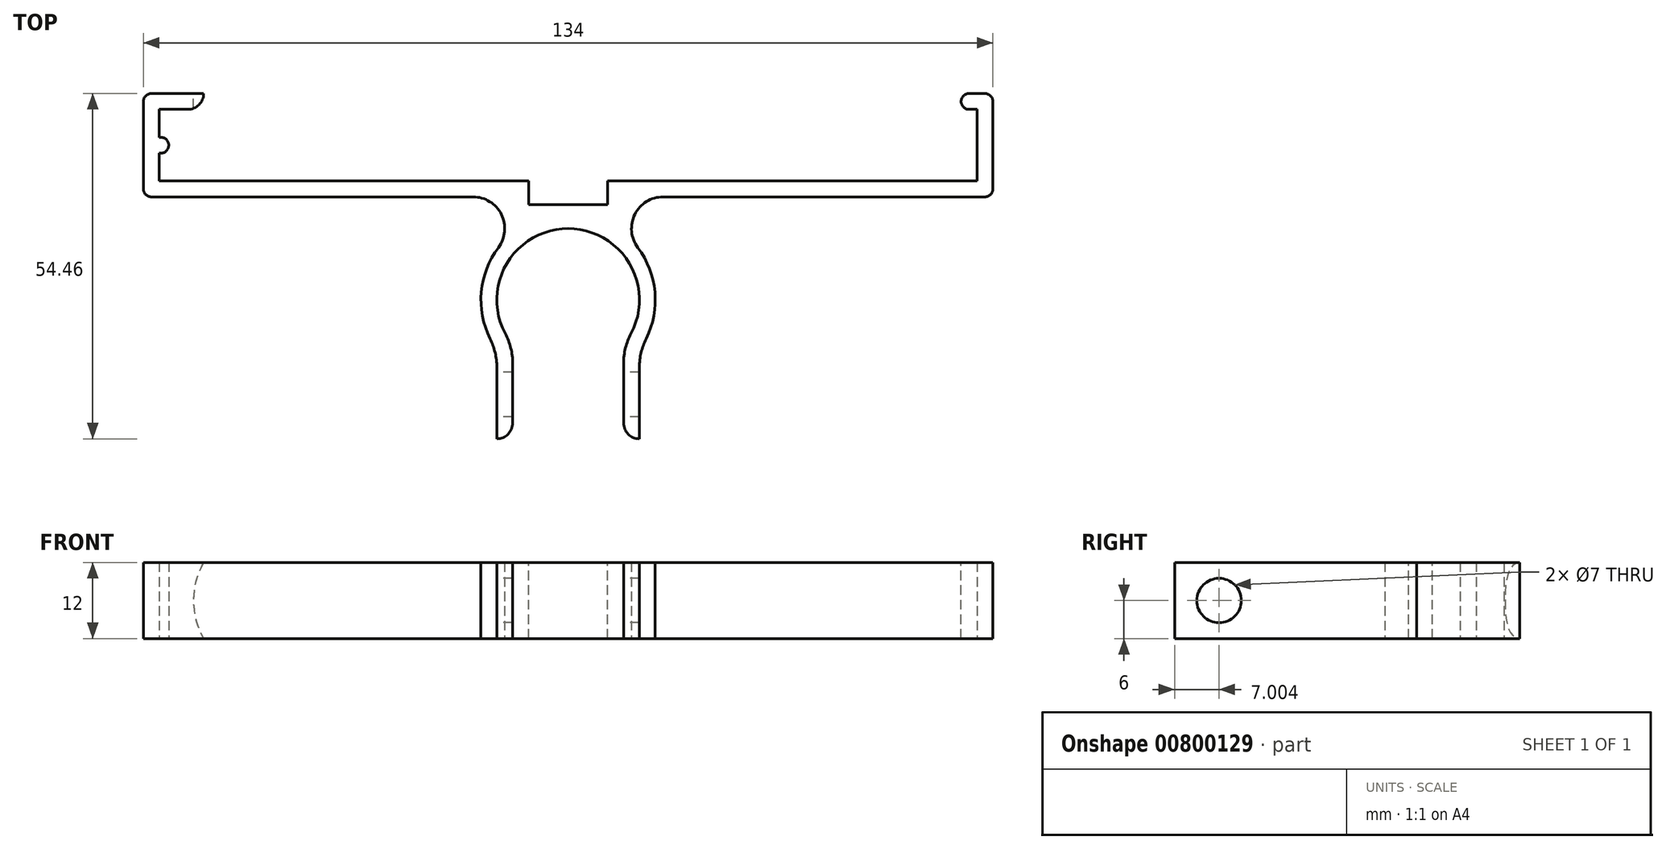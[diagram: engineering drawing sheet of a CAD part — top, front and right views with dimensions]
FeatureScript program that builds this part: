
annotation { "Feature Type Name" : "Feature", "Feature Type Description" : "" }
export const myFeature = defineFeature(function(context is Context, id is Id, definition is map)
    precondition{}
    {
        {
            var Q0;
            Q0=qCreatedBy(makeId("Top.planeOp"),FACE);
            var sketch = newSketch(context, id + "F0", { "sketchPlane" : qUnion([Q0])});
            skArc(sketch, "E0", {"start": v(8.75, -7.07) * mm, "mid": v(0, 11.25) * mm, "end": v(-8.75, -7.07) * mm});
            skArc(sketch, "E1.0", {"start": v(8.75, -10.6) * mm, "mid": v(0, 13.75) * mm, "end": v(-8.75, -10.6) * mm});
            skLineSegment(sketch, "E2", {"start": v(-11.25, 0) * mm, "end": v(-11.25, -21.9) * mm});
            skLineSegment(sketch, "E3", {"start": v(-11.25, -21.9) * mm, "end": v(-8.75, -21.9) * mm});
            skLineSegment(sketch, "E4", {"start": v(-8.75, -21.9) * mm, "end": v(-8.75, -7.07) * mm});
            skPoint(sketch, "E5", {"position": v(-11.25, -7.9) * mm});
            skLineSegment(sketch, "E6.bottom", {"start": v(64.5, 16.25) * mm, "end": v(-64.5, 16.25) * mm});
            skLineSegment(sketch, "E6.top", {"start": v(64.5, 18.75) * mm, "end": v(-64.5, 18.75) * mm});
            skLineSegment(sketch, "E6.left", {"start": v(64.5, 16.25) * mm, "end": v(64.5, 18.75) * mm});
            skPoint(sketch, "E6.middle", {"position": v(0, 17.5) * mm});
            skArc(sketch, "E7", {"start": v(-11, 8.25) * mm, "mid": v(-10.53, 13.49) * mm, "end": v(-15, 16.25) * mm});
            skLineSegment(sketch, "E8.bottom", {"start": v(-64.5, 16.25) * mm, "end": v(-67, 16.25) * mm});
            skLineSegment(sketch, "E8.top", {"start": v(-64.5, 30.05) * mm, "end": v(-67, 30.05) * mm});
            skLineSegment(sketch, "E8.left", {"start": v(-64.5, 18.75) * mm, "end": v(-64.5, 30.05) * mm});
            skLineSegment(sketch, "E8.right", {"start": v(-67, 16.25) * mm, "end": v(-67, 30.05) * mm});
            skLineSegment(sketch, "E9.MirrorCS", {"start": v(8.75, -21.9) * mm, "end": v(8.75, -7.07) * mm});
            skLineSegment(sketch, "E10.MirrorCS", {"start": v(11.25, 0) * mm, "end": v(11.25, -21.9) * mm});
            skLineSegment(sketch, "E11.MirrorCS", {"start": v(11.25, -21.9) * mm, "end": v(8.75, -21.9) * mm});
            skLineSegment(sketch, "E12.MirrorCS", {"start": v(67, 16.25) * mm, "end": v(67, 30.05) * mm});
            skLineSegment(sketch, "E13.MirrorCS", {"start": v(64.5, 16.25) * mm, "end": v(64.5, 30.05) * mm});
            skLineSegment(sketch, "E14.MirrorCS", {"start": v(64.5, 30.05) * mm, "end": v(67, 30.05) * mm});
            skLineSegment(sketch, "E15.MirrorCS", {"start": v(64.5, 16.25) * mm, "end": v(67, 16.25) * mm});
            skLineSegment(sketch, "E16.bottom", {"start": v(-67, 30.05) * mm, "end": v(-57.5, 30.05) * mm});
            skLineSegment(sketch, "E16.top", {"start": v(-67, 32.55) * mm, "end": v(-57.5, 32.55) * mm});
            skLineSegment(sketch, "E16.left", {"start": v(-67, 30.05) * mm, "end": v(-67, 32.55) * mm});
            skLineSegment(sketch, "E16.right", {"start": v(-57.5, 30.05) * mm, "end": v(-57.5, 32.55) * mm});
            skLineSegment(sketch, "E17.trimOffspring", {"start": v(0, 18.75) * mm, "end": v(-64.5, 18.75) * mm});
            skLineSegment(sketch, "E18.bottom", {"start": v(-64.5, 23.15) * mm, "end": v(-63, 23.15) * mm});
            skLineSegment(sketch, "E18.top", {"start": v(-64.5, 25.65) * mm, "end": v(-63, 25.65) * mm});
            skLineSegment(sketch, "E18.left", {"start": v(-64.5, 23.15) * mm, "end": v(-64.5, 25.65) * mm});
            skLineSegment(sketch, "E18.right", {"start": v(-63, 23.15) * mm, "end": v(-63, 25.65) * mm});
            skPoint(sketch, "E19", {"position": v(-64.5, 24.4) * mm});
            skLineSegment(sketch, "E20.bottom", {"start": v(67, 30.05) * mm, "end": v(62, 30.05) * mm});
            skLineSegment(sketch, "E20.top", {"start": v(67, 32.55) * mm, "end": v(62, 32.55) * mm});
            skLineSegment(sketch, "E20.left", {"start": v(67, 30.05) * mm, "end": v(67, 32.55) * mm});
            skLineSegment(sketch, "E20.right", {"start": v(62, 30.05) * mm, "end": v(62, 32.55) * mm});
            skArc(sketch, "E21.MirrorCS", {"start": v(11, 8.25) * mm, "mid": v(10.53, 13.49) * mm, "end": v(15, 16.25) * mm});
            skSolve(sketch);
        }
        {
            var Q0;
            Q0 = qSketchRegion(id + "F0", true);
            extrude(context, id + "F1", {"entities" : qUnion([Q0]), "depth" : 12 * mm, "offsetDistance" : 25 * mm});
        }
        {
            var Q0;
            Q0=makeQuery(id+"F1.opExtrude","SWEPT_FACE",FACE,{"disambiguationData":[OSD([sQuery(id+"F0.wireOp",EDGE,"E2")])]});
            var sketch = newSketch(context, id + "F2", { "sketchPlane" : qUnion([Q0])});
            skCircle(sketch, "E22", {"center": v(14.9, 6) * mm, "radius": 3.5 * mm});
            skSolve(sketch);
        }
        {
            var Q0;
            Q0=makeQuery(id+"F2.imprint","IMPRINT",FACE,{"disambiguationData":[TD([[makeQuery(id+"F2.imprint","IMPRINT",EDGE,{"derivedFrom":sQuery(id+"F2.wireOp",EDGE,"E22")}),1.0]])]});
            var Q1;
            Q1=sQuery(id+"F2.wireOp",EDGE,"E22");
            var Q2;
            Q2=makeQuery(id+"F1.opExtrude","SWEPT_FACE",FACE,{"disambiguationData":[OSD([sQuery(id+"F0.wireOp",EDGE,"E10.MirrorCS")])]});
            extrude(context, id + "F3", {"entities" : qUnion([Q0]), "operationType" : NewBodyOperationType.REMOVE, "surfaceEntities" : qUnion([Q1]), "endBound" : BoundingType.UP_TO_SURFACE, "oppositeDirection" : true, "depth" : 25 * mm, "endBoundEntityFace" : qUnion([Q2]), "offsetDistance" : 25 * mm});
        }
        {
            var Q0;
            Q0=makeQuery(id+"F1.opExtrude","SWEPT_EDGE",EDGE,{"disambiguationData":[OSD([sQuery(id+"F0.wireOp",EDGE,"E0"),sQuery(id+"F0.wireOp",EDGE,"E4")])]});
            var Q1;
            Q1=makeQuery(id+"F1.opExtrude","SWEPT_EDGE",EDGE,{"disambiguationData":[OSD([sQuery(id+"F0.wireOp",EDGE,"E0"),sQuery(id+"F0.wireOp",EDGE,"E9.MirrorCS")])]});
            var Q2;
            Q2=makeQuery(id+"F1.opExtrude","SWEPT_EDGE",EDGE,{"disambiguationData":[OSD([sQuery(id+"F0.wireOp",EDGE,"E1.0"),sQuery(id+"F0.wireOp",EDGE,"E2")])]});
            var Q3;
            Q3=makeQuery(id+"F1.opExtrude","SWEPT_EDGE",EDGE,{"disambiguationData":[OSD([sQuery(id+"F0.wireOp",EDGE,"E1.0"),sQuery(id+"F0.wireOp",EDGE,"E10.MirrorCS")])]});
            fillet(context, id + "F4", {"entities" : qUnion([Q0, Q1, Q2, Q3]), "radius" : 10 * mm, "tangentPropagation" : true, "allowEdgeOverflow" : false});
        }
        {
            var Q0;
            Q0=makeQuery(id+"F1.opExtrude","SWEPT_EDGE",EDGE,{"disambiguationData":[OSD([sQuery(id+"F0.wireOp",EDGE,"E16.bottom"),sQuery(id+"F0.wireOp",EDGE,"E16.right")])]});
            var Q1;
            Q1=makeQuery(id+"F1.opExtrude","SWEPT_EDGE",EDGE,{"disambiguationData":[OSD([sQuery(id+"F0.wireOp",EDGE,"E3"),sQuery(id+"F0.wireOp",EDGE,"E4")])]});
            var Q2;
            Q2=makeQuery(id+"F1.opExtrude","SWEPT_EDGE",EDGE,{"disambiguationData":[OSD([sQuery(id+"F0.wireOp",EDGE,"E9.MirrorCS"),sQuery(id+"F0.wireOp",EDGE,"E11.MirrorCS")])]});
            fillet(context, id + "F5", {"entities" : qUnion([Q0, Q1, Q2]), "radius" : 2.5 * mm, "tangentPropagation" : true, "allowEdgeOverflow" : false});
        }
        {
            var Q0;
            Q0=makeQuery(id+"F1.opExtrude","SWEPT_EDGE",EDGE,{"disambiguationData":[OSD([sQuery(id+"F0.wireOp",EDGE,"E16.top"),sQuery(id+"F0.wireOp",EDGE,"E16.left")])]});
            var Q1;
            Q1=makeQuery(id+"F1.opExtrude","SWEPT_EDGE",EDGE,{"disambiguationData":[OSD([sQuery(id+"F0.wireOp",EDGE,"E8.bottom"),sQuery(id+"F0.wireOp",EDGE,"E8.right")])]});
            var Q2;
            Q2=makeQuery(id+"F1.opExtrude","SWEPT_EDGE",EDGE,{"disambiguationData":[OSD([sQuery(id+"F0.wireOp",EDGE,"E12.MirrorCS"),sQuery(id+"F0.wireOp",EDGE,"E15.MirrorCS")])]});
            var Q3;
            Q3=makeQuery(id+"F1.opExtrude","SWEPT_EDGE",EDGE,{"disambiguationData":[OSD([sQuery(id+"F0.wireOp",EDGE,"E18.bottom"),sQuery(id+"F0.wireOp",EDGE,"E18.right")])]});
            var Q4;
            Q4=makeQuery(id+"F1.opExtrude","SWEPT_EDGE",EDGE,{"disambiguationData":[OSD([sQuery(id+"F0.wireOp",EDGE,"E18.top"),sQuery(id+"F0.wireOp",EDGE,"E18.right")])]});
            var Q5;
            Q5=makeQuery(id+"F1.opExtrude","SWEPT_EDGE",EDGE,{"disambiguationData":[OSD([sQuery(id+"F0.wireOp",EDGE,"E20.top"),sQuery(id+"F0.wireOp",EDGE,"E20.right")])]});
            var Q6;
            Q6=makeQuery(id+"F1.opExtrude","SWEPT_EDGE",EDGE,{"disambiguationData":[OSD([sQuery(id+"F0.wireOp",EDGE,"E20.bottom"),sQuery(id+"F0.wireOp",EDGE,"E20.right")])]});
            var Q7;
            Q7=makeQuery(id+"F1.opExtrude","SWEPT_EDGE",EDGE,{"disambiguationData":[OSD([sQuery(id+"F0.wireOp",EDGE,"E20.top"),sQuery(id+"F0.wireOp",EDGE,"E20.left")])]});
            fillet(context, id + "F6", {"entities" : qUnion([Q0, Q1, Q2, Q3, Q4, Q5, Q6, Q7]), "radius" : 1.25 * mm, "tangentPropagation" : true, "allowEdgeOverflow" : false});
        }
        {
            var Q0;
            Q0=makeQuery(id+"F1.opExtrude","CAP_FACE",FACE,{"disambiguationData":[OSD([sQuery(id+"F0.wireOp",EDGE,"E0"),sQuery(id+"F0.wireOp",EDGE,"E1.0"),sQuery(id+"F0.wireOp",EDGE,"E2"),sQuery(id+"F0.wireOp",EDGE,"E3"),sQuery(id+"F0.wireOp",EDGE,"E4"),sQuery(id+"F0.wireOp",EDGE,"E6.bottom"),sQuery(id+"F0.wireOp",EDGE,"E6.top"),sQuery(id+"F0.wireOp",EDGE,"E7"),sQuery(id+"F0.wireOp",EDGE,"E8.bottom"),sQuery(id+"F0.wireOp",EDGE,"E8.left"),sQuery(id+"F0.wireOp",EDGE,"E8.right"),sQuery(id+"F0.wireOp",EDGE,"ce6fea1b-63f9-4181-841c-8baca797a0580.MirrorCS"),sQuery(id+"F0.wireOp",EDGE,"E9.MirrorCS"),sQuery(id+"F0.wireOp",EDGE,"E10.MirrorCS"),sQuery(id+"F0.wireOp",EDGE,"E11.MirrorCS"),sQuery(id+"F0.wireOp",EDGE,"E12.MirrorCS"),sQuery(id+"F0.wireOp",EDGE,"E13.MirrorCS"),sQuery(id+"F0.wireOp",EDGE,"E15.MirrorCS"),sQuery(id+"F0.wireOp",EDGE,"E16.bottom"),sQuery(id+"F0.wireOp",EDGE,"E16.top"),sQuery(id+"F0.wireOp",EDGE,"E16.left"),sQuery(id+"F0.wireOp",EDGE,"E16.right"),sQuery(id+"F0.wireOp",EDGE,"E18.bottom"),sQuery(id+"F0.wireOp",EDGE,"E18.top"),sQuery(id+"F0.wireOp",EDGE,"E18.right"),sQuery(id+"F0.wireOp",EDGE,"E20.bottom"),sQuery(id+"F0.wireOp",EDGE,"E20.top"),sQuery(id+"F0.wireOp",EDGE,"E20.left"),sQuery(id+"F0.wireOp",EDGE,"E20.right")])],"isStart":false});
            var sketch = newSketch(context, id + "F7", { "sketchPlane" : qUnion([Q0])});
            skLineSegment(sketch, "E23.bottom", {"start": v(6.25, 18.75) * mm, "end": v(-6.25, 18.75) * mm});
            skLineSegment(sketch, "E23.top", {"start": v(6.25, 15) * mm, "end": v(-6.25, 15) * mm});
            skLineSegment(sketch, "E23.left", {"start": v(6.25, 18.75) * mm, "end": v(6.25, 15) * mm});
            skLineSegment(sketch, "E23.right", {"start": v(-6.25, 18.75) * mm, "end": v(-6.25, 15) * mm});
            skPoint(sketch, "E23.middle", {"position": v(0, 16.87) * mm});
            skSolve(sketch);
        }
        {
            var Q0;
            Q0 = qSketchRegion(id + "F7", true);
            extrude(context, id + "F8", {"entities" : qUnion([Q0]), "operationType" : NewBodyOperationType.REMOVE, "endBound" : BoundingType.UP_TO_NEXT, "oppositeDirection" : true, "depth" : 25 * mm, "offsetDistance" : 25 * mm});
        }
        {
            var Q0;
            Q0=makeQuery(id+"F1.opExtrude","SWEPT_FACE",FACE,{"disambiguationData":[OSD([sQuery(id+"F0.wireOp",EDGE,"E16.top")])]});
            var sketch = newSketch(context, id + "F9", { "sketchPlane" : qUnion([Q0])});
            skArc(sketch, "E24", {"start": v(57.5, 0) * mm, "mid": v(59.1, 6) * mm, "end": v(57.5, 12) * mm});
            skSolve(sketch);
        }
        {
            var Q0;
            Q0=makeQuery(id+"F9.imprint","IMPRINT",FACE,{"disambiguationData":[TD([[makeQuery(id+"F9.imprint","IMPRINT",EDGE,{"derivedFrom":sQuery(id+"F9.wireOp",EDGE,"E24")}),1.0]])]});
            var Q1;
            Q1=makeQuery(id+"F1.opExtrude","SWEPT_FACE",FACE,{"disambiguationData":[OSD([sQuery(id+"F0.wireOp",EDGE,"E16.bottom")])]});
            extrude(context, id + "F10", {"entities" : qUnion([Q0]), "operationType" : NewBodyOperationType.REMOVE, "endBound" : BoundingType.UP_TO_SURFACE, "oppositeDirection" : true, "depth" : 25 * mm, "endBoundEntityFace" : qUnion([Q1]), "offsetDistance" : 25 * mm});
        }
    });
